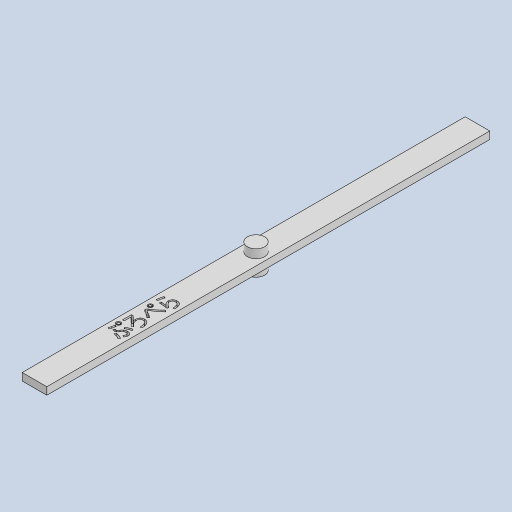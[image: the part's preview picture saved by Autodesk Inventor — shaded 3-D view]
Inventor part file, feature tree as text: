
AUTODESK INVENTOR PART (.ipt)
format: ipt  version: 2023 (Build 270158000, 158)  size: 319,488 bytes
history: native  units: mm
features: extrude x3, sketch x3, other x1
ambient origin geometry x8: Origin, YZ Plane, XZ Plane, XY Plane, X Axis, Y Axis, Z Axis, Center Point
bodies: Body1 (feature_tree)
feature tree (7):
  other  "ソリッド1"
  extrude  "押し出し1"  Depth=7.0mm
  extrude  "押し出し2"  Depth=10.0mm TaperAngle=0.0deg
  extrude  "押し出し3"  Depth=10.0mm
  sketch  "スケッチ1"
  sketch  "スケッチ2"
  sketch  "スケッチ3"
